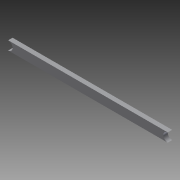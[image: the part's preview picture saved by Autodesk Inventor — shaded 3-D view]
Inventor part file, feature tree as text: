
AUTODESK INVENTOR PART (.ipt)
format: ipt  version: 2011 (Build 150239000, 239)  size: 81,920 bytes
history: native  units: in
note: dims shown in document units (in); Inventor stores cm internally (conversion verified against a paired STEP export)
features: extrude x3, sketch x3
ambient origin geometry x8: Origin, YZ Plane, XZ Plane, XY Plane, X Axis, Y Axis, Z Axis, Center Point
bodies: Solid1 (feature_tree)
feature tree (6):
  extrude  "Extrusion1"  Depth=0.25in
  extrude  "Extrusion2"  Depth=0.125in
  extrude  "Extrusion3"  Depth=0.125in TaperAngle=0.0deg
  sketch  "Sketch1"  dims[d0=4.5in d1=0.25in]
  sketch  "Sketch2"  dims[d2=0.25in d3=0.0in d4=0.125in]
  sketch  "Sketch3"  dims[d5=0.25in d6=0.0in d7=0.125in d8=0.0in]
